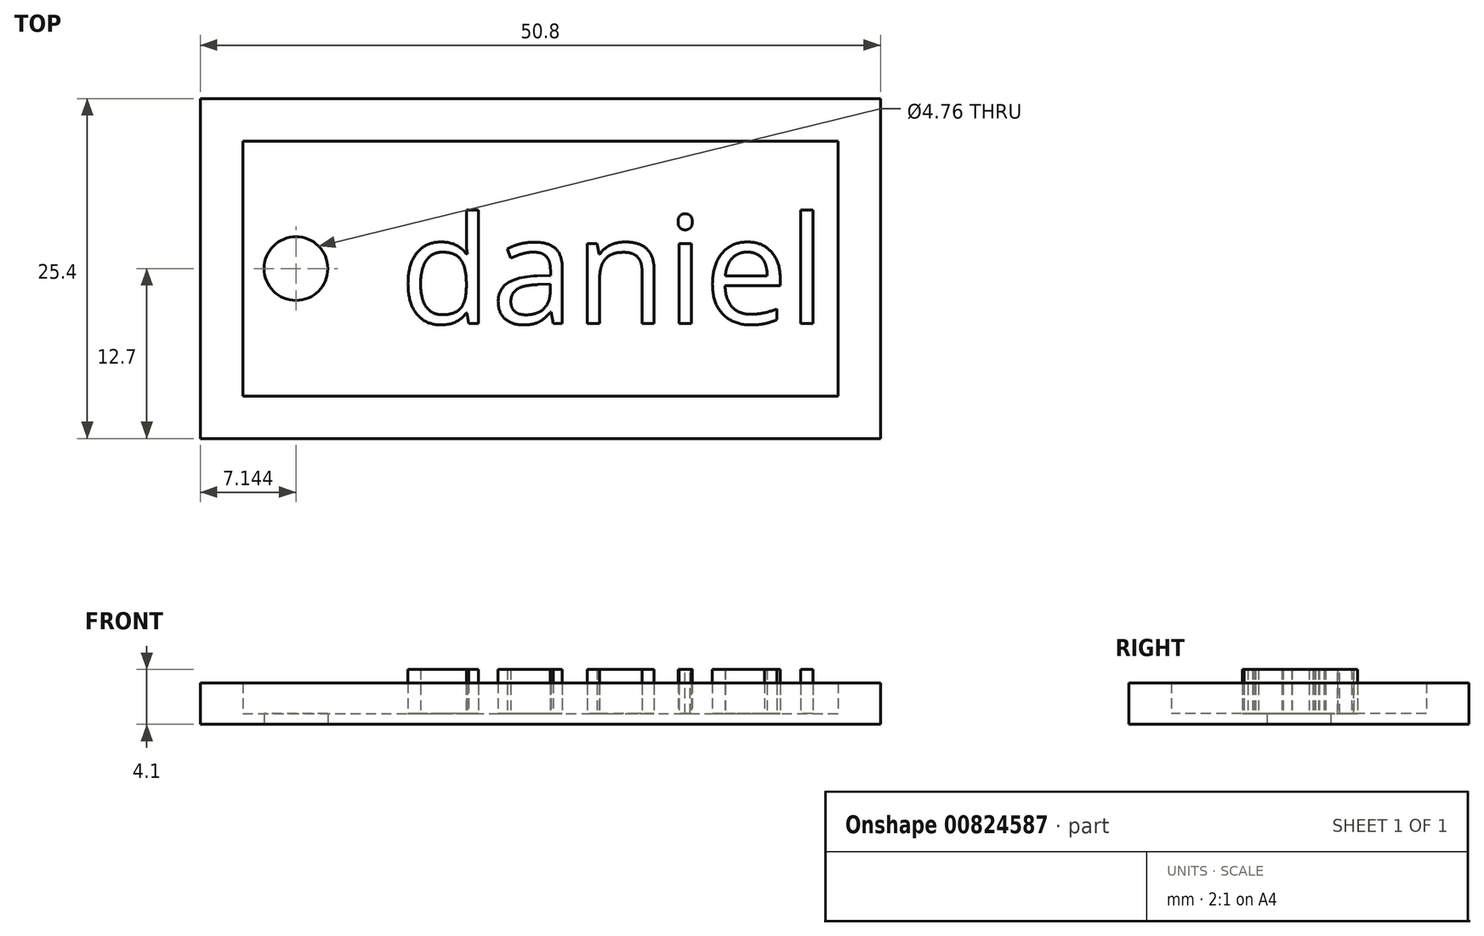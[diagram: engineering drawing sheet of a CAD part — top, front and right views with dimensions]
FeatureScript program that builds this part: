
annotation { "Feature Type Name" : "Feature", "Feature Type Description" : "" }
export const myFeature = defineFeature(function(context is Context, id is Id, definition is map)
    precondition{}
    {
        {
            var Q0;
            Q0=qCreatedBy(makeId("Top.planeOp"),FACE);
            var sketch = newSketch(context, id + "F0", { "sketchPlane" : qUnion([Q0])});
            skLineSegment(sketch, "E0.bottom", {"start": v(0, 0) * mm, "end": v(50.8, 0) * mm});
            skLineSegment(sketch, "E0.top", {"start": v(0, 25.4) * mm, "end": v(50.8, 25.4) * mm});
            skLineSegment(sketch, "E0.left", {"start": v(0, 0) * mm, "end": v(0, 25.4) * mm});
            skLineSegment(sketch, "E0.right", {"start": v(50.8, 0) * mm, "end": v(50.8, 25.4) * mm});
            skCircle(sketch, "E1", {"center": v(7.14, 12.7) * mm, "radius": 2.38 * mm});
            skPoint(sketch, "E1.centerSnap0", {"position": v(0, 12.7) * mm});
            skLineSegment(sketch, "E2.bottom", {"start": v(3.17, 22.23) * mm, "end": v(47.63, 22.23) * mm});
            skLineSegment(sketch, "E2.top", {"start": v(3.18, 3.18) * mm, "end": v(47.63, 3.18) * mm});
            skLineSegment(sketch, "E2.left", {"start": v(3.17, 22.23) * mm, "end": v(3.18, 3.18) * mm});
            skLineSegment(sketch, "E2.right", {"start": v(47.63, 22.23) * mm, "end": v(47.63, 3.18) * mm});
            skSolve(sketch);
        }
        {
            var Q0;
            Q0 = qSketchRegion(id + "F0", true);
            extrude(context, id + "F1", {"entities" : qUnion([Q0]), "depth" : 2.3 * mm, "offsetDistance" : 25.4 * mm});
        }
        {
            var Q0;
            Q0=makeQuery(id+"F0.imprint","IMPRINT",FACE,{"disambiguationData":[TD([[makeQuery(id+"F0.imprint","IMPRINT",EDGE,{"derivedFrom":sQuery(id+"F0.wireOp",EDGE,"E1")}),-1.0]])]});
            var Q1;
            Q1=makeQuery(id+"F1.opExtrude","CAP_FACE",FACE,{"disambiguationData":[OSD([sQuery(id+"F0.wireOp",EDGE,"E0.bottom"),sQuery(id+"F0.wireOp",EDGE,"E0.top"),sQuery(id+"F0.wireOp",EDGE,"E0.left"),sQuery(id+"F0.wireOp",EDGE,"E0.right"),sQuery(id+"F0.wireOp",EDGE,"E2.bottom"),sQuery(id+"F0.wireOp",EDGE,"E2.top"),sQuery(id+"F0.wireOp",EDGE,"E2.left"),sQuery(id+"F0.wireOp",EDGE,"E2.right")])],"isStart":false});
            extrude(context, id + "F2", {"entities" : qUnion([Q0, Q1]), "operationType" : NewBodyOperationType.ADD, "depth" : 0.8 * mm, "offsetDistance" : 25.4 * mm});
        }
        {
            var Q0;
            Q0=makeQuery(id+"F2.opExtrude","CAP_FACE",FACE,{"disambiguationData":[OSD([sQuery(id+"F0.wireOp",EDGE,"E1"),sQuery(id+"F0.wireOp",EDGE,"E2.bottom"),sQuery(id+"F0.wireOp",EDGE,"E2.top"),sQuery(id+"F0.wireOp",EDGE,"E2.left"),sQuery(id+"F0.wireOp",EDGE,"E2.right")])],"isStart":false});
            var sketch = newSketch(context, id + "F3", { "sketchPlane" : qUnion([Q0])});
            skText(sketch, "E3", { "text": "daniel", "fontName": "OpenSans-Regular.ttf"});
            const initialGuessF3  = {"E3": [0.01489, 0.0086, 1, 0, 0.00804]};
            skSetInitialGuess(sketch, initialGuessF3);
            skSolve(sketch);
        }
        {
            var Q0;
            Q0 = qSketchRegion(id + "F3", true);
            extrude(context, id + "F4", {"entities" : qUnion([Q0]), "operationType" : NewBodyOperationType.ADD, "depth" : 3.3 * mm, "offsetDistance" : 25.4 * mm});
        }
    });
